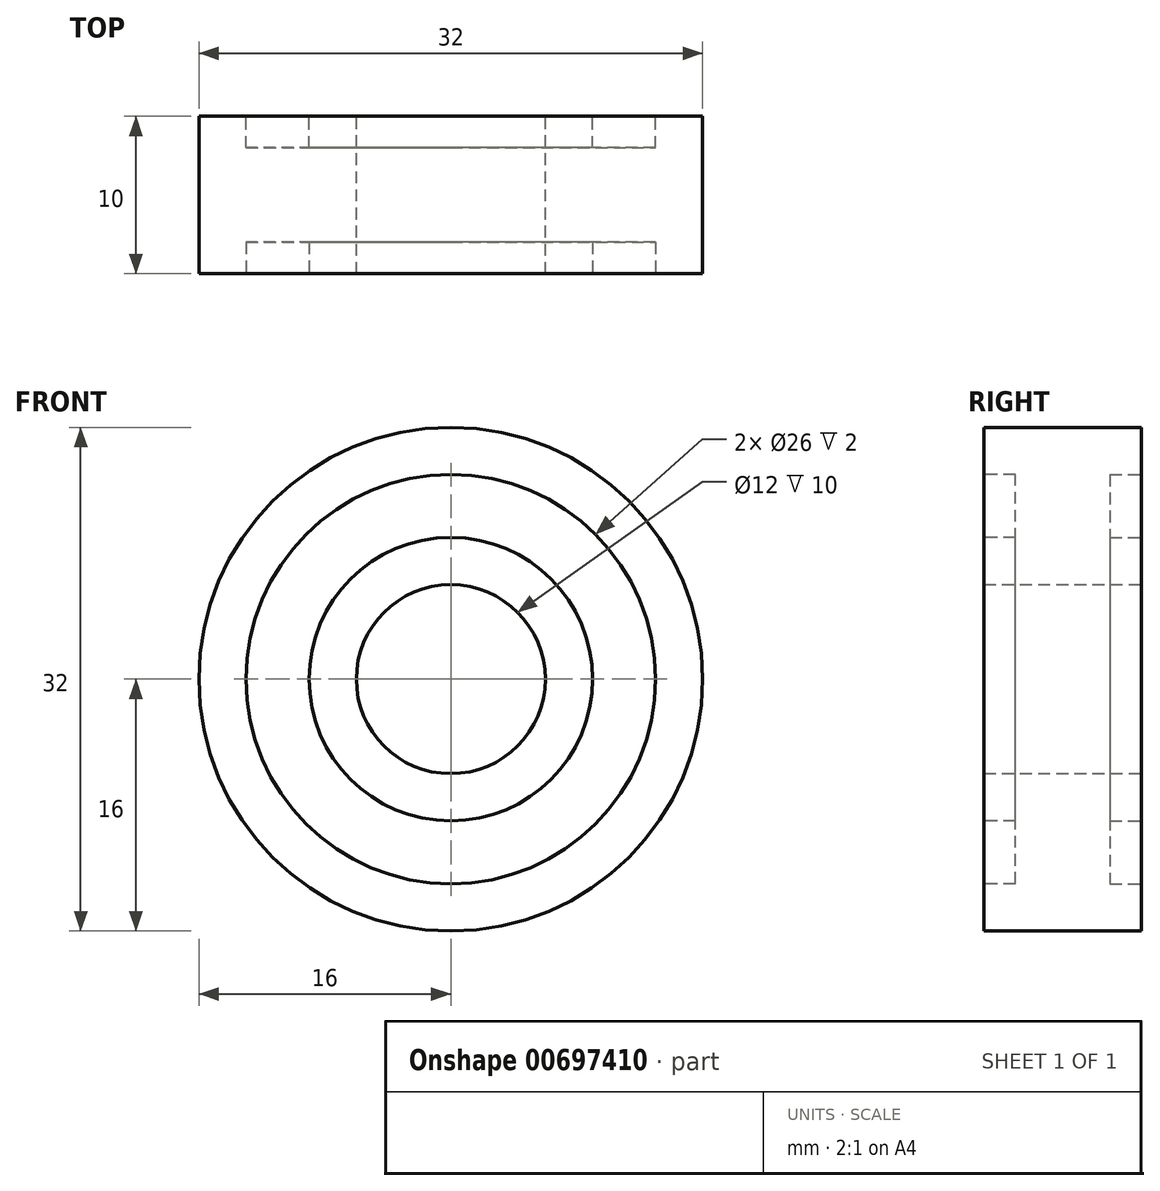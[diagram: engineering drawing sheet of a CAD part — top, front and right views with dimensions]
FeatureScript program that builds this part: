
annotation { "Feature Type Name" : "Feature", "Feature Type Description" : "" }
export const myFeature = defineFeature(function(context is Context, id is Id, definition is map)
    precondition{}
    {
        {
            var Q0;
            Q0=qCreatedBy(makeId("Front.planeOp"),FACE);
            var sketch = newSketch(context, id + "F0", { "sketchPlane" : qUnion([Q0])});
            skCircle(sketch, "E0", {"center": v(0, 0) * mm, "radius": 16 * mm});
            skCircle(sketch, "E1", {"center": v(0, 0) * mm, "radius": 6 * mm});
            skSolve(sketch);
        }
        {
            var Q0;
            Q0=makeQuery(id+"F0.imprint","IMPRINT",FACE,{"disambiguationData":[TD([[makeQuery(id+"F0.imprint","IMPRINT",EDGE,{"derivedFrom":sQuery(id+"F0.wireOp",EDGE,"E0")}),1.0]])]});
            extrude(context, id + "F1", {"entities" : qUnion([Q0]), "depth" : 10 * mm, "offsetDistance" : 25 * mm});
        }
        {
            var Q0;
            Q0=makeQuery(id+"F1.opExtrude","CAP_FACE",FACE,{"disambiguationData":[OSD([sQuery(id+"F0.wireOp",EDGE,"E0"),sQuery(id+"F0.wireOp",EDGE,"E1")])],"isStart":false});
            var sketch = newSketch(context, id + "F2", { "sketchPlane" : qUnion([Q0])});
            skCircle(sketch, "E2", {"center": v(0, 0) * mm, "radius": 13 * mm});
            skCircle(sketch, "E3", {"center": v(0, 0) * mm, "radius": 9 * mm});
            skSolve(sketch);
        }
        {
            var Q0;
            Q0=makeQuery(id+"F2.imprint","IMPRINT",FACE,{"disambiguationData":[TD([[makeQuery(id+"F2.imprint","IMPRINT",EDGE,{"derivedFrom":sQuery(id+"F2.wireOp",EDGE,"E2")}),1.0]])]});
            extrude(context, id + "F3", {"entities" : qUnion([Q0]), "operationType" : NewBodyOperationType.REMOVE, "oppositeDirection" : true, "depth" : 2 * mm, "offsetDistance" : 25 * mm});
        }
        {
            var Q0;
            Q0=makeQuery(id+"F1.opExtrude","CAP_FACE",FACE,{"disambiguationData":[OSD([sQuery(id+"F0.wireOp",EDGE,"E0"),sQuery(id+"F0.wireOp",EDGE,"E1")])],"isStart":true});
            var sketch = newSketch(context, id + "F4", { "sketchPlane" : qUnion([Q0])});
            skCircle(sketch, "E4", {"center": v(0, 0) * mm, "radius": 9 * mm});
            skCircle(sketch, "E5", {"center": v(0, 0) * mm, "radius": 13 * mm});
            skSolve(sketch);
        }
        {
            var Q0;
            Q0=makeQuery(id+"F4.imprint","IMPRINT",FACE,{"disambiguationData":[TD([[makeQuery(id+"F4.imprint","IMPRINT",EDGE,{"derivedFrom":sQuery(id+"F4.wireOp",EDGE,"E4")}),-1.0]])]});
            extrude(context, id + "F5", {"entities" : qUnion([Q0]), "operationType" : NewBodyOperationType.REMOVE, "oppositeDirection" : true, "depth" : 2 * mm, "offsetDistance" : 25 * mm});
        }
    });
